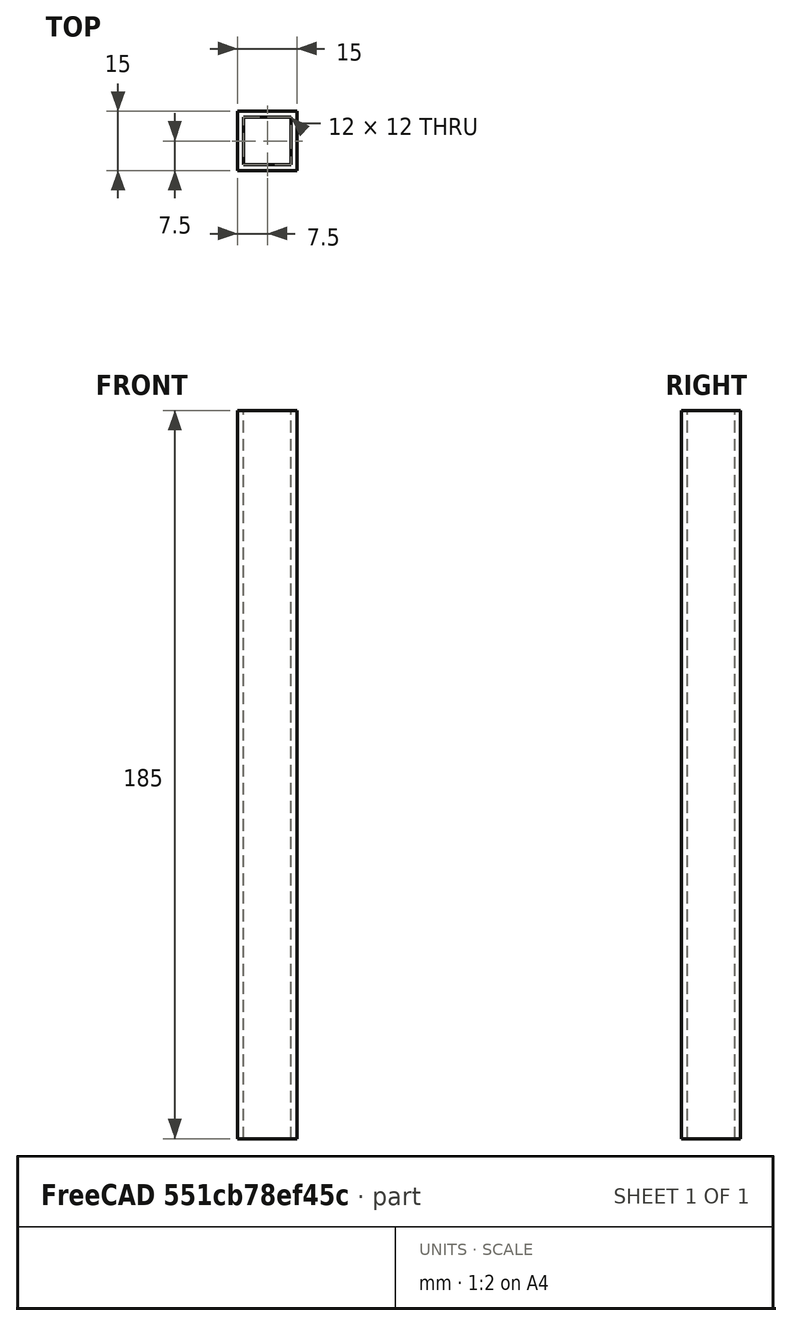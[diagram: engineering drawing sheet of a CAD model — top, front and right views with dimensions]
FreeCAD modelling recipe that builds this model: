
FCSTD DOCUMENT  (FreeCAD 0.16R6698 (Git))
Label: Tube 195
License: All rights reserved
LicenseURL: http://en.wikipedia.org/wiki/All_rights_reserved
objects: Sketcher::SketchObject×1, PartDesign::Pad×1
note: 3 computed .brp shape members not serialized (recipe doc carries the construction recipe); baked Part::Feature solids carry a one-line shape summary decoded from their .brp

FEATURE [Sketcher::SketchObject] Sketch
  sketch-geometry (8):
    g0: LineSegment StartX=-7.5 StartY=7.5 StartZ=0 EndX=7.5 EndY=7.5 EndZ=0
    g1: LineSegment StartX=7.5 StartY=7.5 StartZ=0 EndX=7.5 EndY=-7.5 EndZ=0
    g2: LineSegment StartX=7.5 StartY=-7.5 StartZ=0 EndX=-7.5 EndY=-7.5 EndZ=0
    g3: LineSegment StartX=-7.5 StartY=-7.5 StartZ=0 EndX=-7.5 EndY=7.5 EndZ=0
    g4: LineSegment StartX=-6 StartY=6 StartZ=0 EndX=6 EndY=6 EndZ=0
    g5: LineSegment StartX=6 StartY=6 StartZ=0 EndX=6 EndY=-6 EndZ=0
    g6: LineSegment StartX=6 StartY=-6 StartZ=0 EndX=-6 EndY=-6 EndZ=0
    g7: LineSegment StartX=-6 StartY=-6 StartZ=0 EndX=-6 EndY=6 EndZ=0
  constraints (24):
    c: Coincident(g0,g1)
    c: Coincident(g1,g2)
    c: Coincident(g2,g3)
    c: Coincident(g3,g0)
    c: Horizontal(g0)
    c: Horizontal(g2)
    c: Vertical(g1)
    c: Vertical(g3)
    c: DistanceX(g0,g0) = 15
    c: DistanceY(g1,g1) = 15
    c: DistanceY(g1,g-1) = 7.5
    c: DistanceX(g-1,g1) = 7.5
    c: Coincident(g4,g5)
    c: Coincident(g5,g6)
    c: Coincident(g6,g7)
    c: Coincident(g7,g4)
    c: Horizontal(g4)
    c: Horizontal(g6)
    c: Vertical(g5)
    c: Vertical(g7)
    c: DistanceX(g5,g1) = 1.5
    c: DistanceY(g1,g5) = 1.5
    c: DistanceX(g2,g6) = 1.5
    c: DistanceY(g4,g0) = 1.5
FEATURE [PartDesign::Pad] Pad
  Length = 185
  Length2 = 100
  Sketch = -> Sketch
  Type = 0
